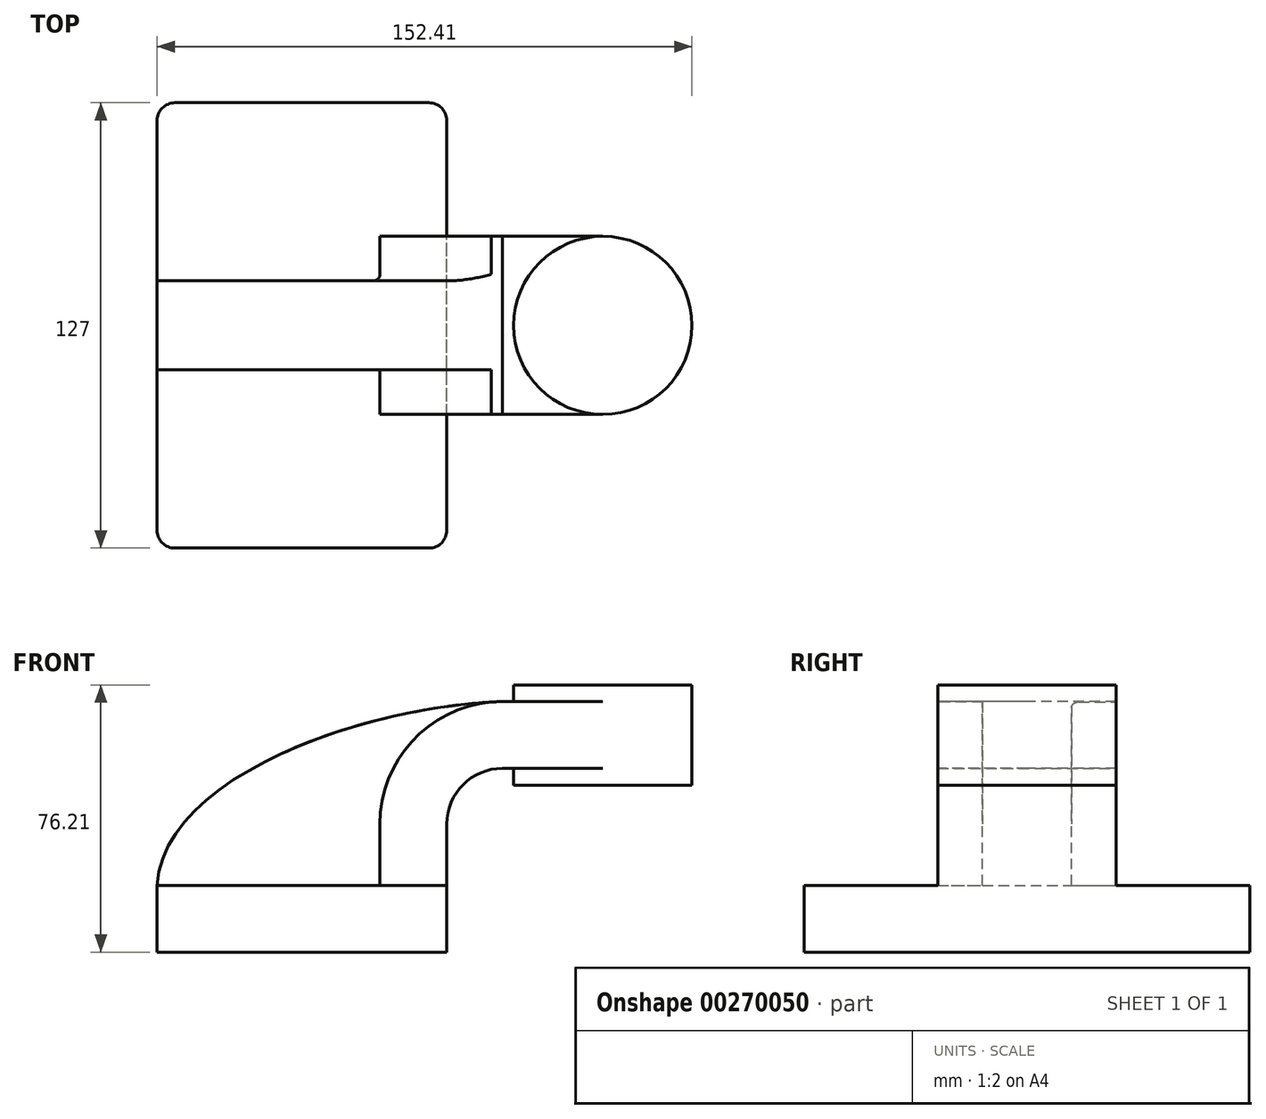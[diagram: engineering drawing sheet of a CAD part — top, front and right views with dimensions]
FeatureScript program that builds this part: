
annotation { "Feature Type Name" : "Feature", "Feature Type Description" : "" }
export const myFeature = defineFeature(function(context is Context, id is Id, definition is map)
    precondition{}
    {
        {
            var Q0;
            Q0=qCreatedBy(makeId("Front.planeOp"),FACE);
            var sketch = newSketch(context, id + "F0", { "sketchPlane" : qUnion([Q0])});
            skLineSegment(sketch, "E0.rect.bottom", {"start": v(-41.28, 9.52) * mm, "end": v(41.28, 9.52) * mm});
            skLineSegment(sketch, "E0.rect.top", {"start": v(-41.28, -9.52) * mm, "end": v(41.28, -9.52) * mm});
            skLineSegment(sketch, "E0.rect.left", {"start": v(-41.28, 9.52) * mm, "end": v(-41.28, -9.52) * mm});
            skLineSegment(sketch, "E0.rect.right", {"start": v(41.28, 9.52) * mm, "end": v(41.28, -9.52) * mm});
            skPoint(sketch, "E0.rect.middle", {"position": v(0, 0) * mm});
            skLineSegment(sketch, "E1", {"start": v(41.28, 9.52) * mm, "end": v(41.28, 27) * mm});
            skArc(sketch, "E2", {"start": v(41.28, 27) * mm, "mid": v(45.92, 38.23) * mm, "end": v(57.15, 42.88) * mm});
            skLineSegment(sketch, "E3", {"start": v(57.15, 42.88) * mm, "end": v(85.72, 42.88) * mm});
            skLineSegment(sketch, "E4.rect.bottom", {"start": v(60.32, 38.1) * mm, "end": v(111.12, 38.1) * mm});
            skLineSegment(sketch, "E4.rect.top", {"start": v(60.32, 66.68) * mm, "end": v(111.12, 66.68) * mm});
            skLineSegment(sketch, "E4.rect.left", {"start": v(60.32, 38.1) * mm, "end": v(60.32, 66.68) * mm});
            skLineSegment(sketch, "E4.rect.right", {"start": v(111.13, 38.1) * mm, "end": v(111.12, 66.68) * mm});
            skPoint(sketch, "E4.rect.middle", {"position": v(85.72, 52.39) * mm});
            skLineSegment(sketch, "E5.0", {"start": v(57.15, 61.93) * mm, "end": v(85.72, 61.93) * mm});
            skArc(sketch, "E5.1", {"start": v(22.23, 27) * mm, "mid": v(32.45, 51.7) * mm, "end": v(57.15, 61.93) * mm});
            skLineSegment(sketch, "E5.2", {"start": v(22.23, 9.52) * mm, "end": v(22.23, 27) * mm});
            skLineSegment(sketch, "E6", {"start": v(85.72, 38.1) * mm, "end": v(85.72, 66.68) * mm});
            skFitSpline(sketch, "E7", {"points": [v(-41.28, 9.53) * mm, v(57.15, 61.93) * mm], "startDerivative": vector(5.2, 92.34) * mm, "endDerivative": vector(120.92, 4.22) * mm});
            skSolve(sketch);
        }
        {
            var Q0;
            Q0=makeQuery(id+"F0.imprint","IMPRINT",FACE,{"disambiguationData":[TD([[makeQuery(id+"F0.imprint","IMPRINT",EDGE,{"derivedFrom":sQuery(id+"F0.wireOp",EDGE,"E0.rect.top")}),1.0]])]});
            extrude(context, id + "F1", {"entities" : qUnion([Q0]), "endBound" : BoundingType.SYMMETRIC, "depth" : 127 * mm});
        }
        {
            var Q0;
            {var subQ9=sQuery(id+"F0.wireOp",EDGE,"E1");Q0=makeQuery(id+"F0.imprint","IMPRINT",FACE,{"disambiguationData":[TD([[makeQuery(id+"F0.imprint","IMPRINT",EDGE,{"derivedFrom":subQ9}),1.0]])]});}
            var Q1;
            {var subQ0=sQuery(id+"F0.wireOp",EDGE,"E6");var subQ1=sQuery(id+"F0.wireOp",EDGE,"E3");var subQ2=makeQuery(id+"F0.imprint","INTERSECT",VERTEX,{"derivedFrom":[subQ1,subQ0]});Q1=makeQuery(id+"F0.imprint","IMPRINT",FACE,{"disambiguationData":[TD([[makeQuery(id+"F0.imprint","IMPRINT",EDGE,{"disambiguationData":[TD([[subQ2,1.0]])],"derivedFrom":subQ1}),1.0]])]});}
            extrude(context, id + "F2", {"entities" : qUnion([Q0, Q1]), "operationType" : NewBodyOperationType.ADD, "endBound" : BoundingType.SYMMETRIC, "depth" : 50.8 * mm});
        }
        {
            var Q0;
            {var subQ3=sQuery(id+"F0.wireOp",EDGE,"E5.2");Q0=makeQuery(id+"F0.imprint","IMPRINT",FACE,{"disambiguationData":[TD([[makeQuery(id+"F0.imprint","IMPRINT",EDGE,{"derivedFrom":subQ3}),1.0]])]});}
            var Q1;
            {var subQ3=sQuery(id+"F0.wireOp",EDGE,"E5.2");Q1=makeQuery(id+"F0.imprint","IMPRINT",FACE,{"disambiguationData":[TD([[makeQuery(id+"F0.imprint","IMPRINT",EDGE,{"derivedFrom":subQ3}),1.0]])]});}
            extrude(context, id + "F3", {"entities" : qUnion([Q0, Q1]), "operationType" : NewBodyOperationType.ADD, "endBound" : BoundingType.SYMMETRIC, "depth" : 25.4 * mm});
        }
        {
            var Q0;
            {var subQ5=sQuery(id+"F0.wireOp",EDGE,"E4.rect.right");Q0=makeQuery(id+"F0.imprint","IMPRINT",FACE,{"disambiguationData":[TD([[makeQuery(id+"F0.imprint","IMPRINT",EDGE,{"derivedFrom":subQ5}),1.0]])]});}
            var Q1;
            Q1=sQuery(id+"F0.wireOp",EDGE,"E6");
            revolve(context, id + "F4", {"operationType" : NewBodyOperationType.ADD, "entities" : qUnion([Q0]), "axis" : qUnion([Q1]), "revolveType" : RevolveType.FULL});
        }
        {
            var Q0;
            Q0=makeQuery(id+"F1.opExtrude","CAP_EDGE",EDGE,{"disambiguationData":[OSD([sQuery(id+"F0.wireOp",EDGE,"E0.rect.right")])],"isStart":false});
            var Q1;
            Q1=makeQuery(id+"F1.opExtrude","CAP_EDGE",EDGE,{"disambiguationData":[OSD([sQuery(id+"F0.wireOp",EDGE,"E0.rect.left")])],"isStart":false});
            var Q2;
            Q2=makeQuery(id+"F1.opExtrude","CAP_EDGE",EDGE,{"disambiguationData":[OSD([sQuery(id+"F0.wireOp",EDGE,"E0.rect.right")])],"isStart":true});
            var Q3;
            Q3=makeQuery(id+"F1.opExtrude","CAP_EDGE",EDGE,{"disambiguationData":[OSD([sQuery(id+"F0.wireOp",EDGE,"E0.rect.left")])],"isStart":true});
            fillet(context, id + "F5", {"entities" : qUnion([Q0, Q1, Q2, Q3]), "radius" : 5.08 * mm, "tangentPropagation" : true, "allowEdgeOverflow" : false});
        }
        {
            var Q0;
            Q0=makeQuery(id+"F3.opExtrude","CAP_EDGE",EDGE,{"disambiguationData":[OSD([sQuery(id+"F0.wireOp",EDGE,"E5.1")])],"isStart":true});
            var Q1;
            Q1=makeQuery(id+"F3.opExtrude","CAP_EDGE",EDGE,{"disambiguationData":[OSD([sQuery(id+"F0.wireOp",EDGE,"E5.1")])],"isStart":false});
            fillet(context, id + "F6", {"entities" : qUnion([Q0, Q1]), "radius" : 2 * mm, "tangentPropagation" : true, "allowEdgeOverflow" : false});
        }
    });
